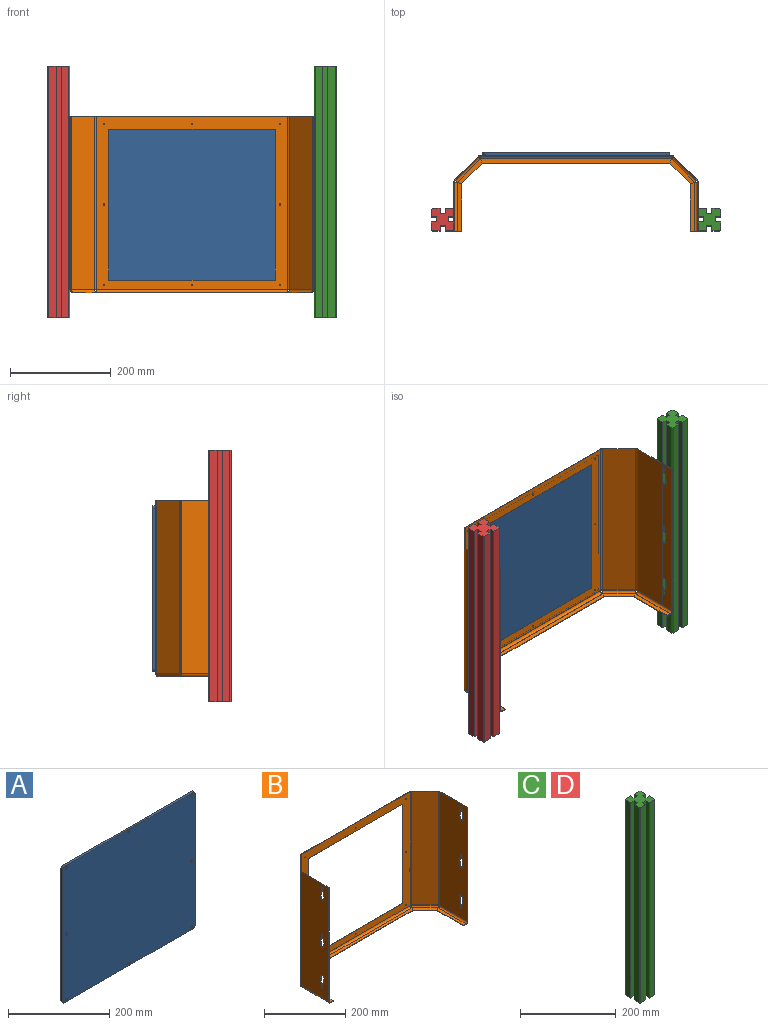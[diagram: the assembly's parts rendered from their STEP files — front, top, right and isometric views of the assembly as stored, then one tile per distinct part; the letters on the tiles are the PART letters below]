
ASSEMBLY  parts=4 mates=3
PART A: 26 faces, bbox 370x5x330 mm
  f0: plane 360x5mm, normal (0,0,-1), area 1800mm2, adj f4,f5,f22,f25
  f1: plane 320x5mm, normal (1,0,0), area 1600mm2, adj f4,f5,f22,f23
  f2: plane 360x5mm, normal (0,0,1), area 1800mm2, adj f4,f5,f23,f24
  f3: plane 320x5mm, normal (-1,0,0), area 1600mm2, adj f4,f5,f24,f25
  f4: plane 370x330mm, normal (0,-1,0), area 121794.8mm2, adj f0,f1,f2,f3,f7,f9,f11,f13
  f5: plane 370x330mm, normal (0,1,0), area 122005.9mm2, adj f0,f1,f2,f3,f6,f8,f10,f12
  f6: cylinder r=1.7mm len=3.4mm, axis (0,-1,0), area 35.7mm2, adj f5,f7
  f7: cone r=1.7mm half-angle=45deg, axis (0,-1,0), area 37.3mm2, adj f4,f6
  f8: cylinder r=1.7mm len=3.4mm, axis (0,-1,0), area 35.7mm2, adj f5,f9
  f9: cone r=1.7mm half-angle=45deg, axis (0,-1,0), area 37.3mm2, adj f4,f8
  f10: cylinder r=1.7mm len=3.4mm, axis (0,-1,0), area 35.7mm2, adj f5,f11
  f11: cone r=1.7mm half-angle=45deg, axis (0,-1,0), area 37.3mm2, adj f4,f10
  f12: cylinder r=1.7mm len=3.4mm, axis (0,-1,0), area 35.7mm2, adj f5,f13
  f13: cone r=1.7mm half-angle=45deg, axis (0,-1,0), area 37.3mm2, adj f4,f12
  f14: cylinder r=1.7mm len=3.4mm, axis (0,-1,0), area 35.7mm2, adj f5,f15
  f15: cone r=1.7mm half-angle=45deg, axis (0,-1,0), area 37.3mm2, adj f4,f14
  f16: cylinder r=1.7mm len=3.4mm, axis (0,-1,0), area 35.7mm2, adj f5,f17
  f17: cone r=1.7mm half-angle=45deg, axis (0,-1,0), area 37.3mm2, adj f4,f16
  f18: cylinder r=1.7mm len=3.4mm, axis (0,-1,0), area 35.7mm2, adj f5,f19
  f19: cone r=1.7mm half-angle=45deg, axis (0,-1,0), area 37.3mm2, adj f4,f18
  f20: cylinder r=1.7mm len=3.4mm, axis (0,-1,0), area 35.7mm2, adj f5,f21
  f21: cone r=1.7mm half-angle=45deg, axis (0,-1,0), area 37.3mm2, adj f4,f20
  f22: cylinder r=5mm len=5mm, axis (0,-1,0), area 39.3mm2, adj f0,f1,f4,f5
  f23: cylinder r=5mm len=5mm, axis (0,1,0), area 39.3mm2, adj f1,f2,f4,f5
  f24: cylinder r=5mm len=5mm, axis (0,-1,0), area 39.3mm2, adj f2,f3,f4,f5
  f25: cylinder r=5mm len=5mm, axis (0,1,0), area 39.3mm2, adj f0,f3,f4,f5
PART B: 146 faces, bbox 485x150x350 mm
  f0: plane 1.2x0.01mm, normal (0,0,-1), area 0mm2, adj f27,f28,f121,f142
  f1: plane 97.43x1.2mm, normal (0,0,1), area 116.9mm2, adj f26,f27,f28,f120
  f2: cylinder r=5mm len=4.68mm, axis (1,0,0), area 7.3mm2, adj f3,f25,f27,f28
  f3: plane 18x1.2mm, normal (0,-1,0), area 21.6mm2, adj f2,f4,f27,f28
  f4: cylinder r=5mm len=10mm, axis (1,0,0), area 18.8mm2, adj f3,f5,f27,f28
  f5: plane 18x1.2mm, normal (0,1,0), area 21.6mm2, adj f4,f6,f27,f28
  f6: cylinder r=5mm len=4.68mm, axis (1,0,0), area 7.3mm2, adj f5,f7,f27,f28
  f7: plane 10.32x1.2mm, normal (0,1,0), area 12.4mm2, adj f6,f8,f27,f28
  f8: cylinder r=1.75mm len=3.5mm, axis (1,0,0), area 6.6mm2, adj f7,f25,f27,f28
  f9: cylinder r=5mm len=4.68mm, axis (1,0,0), area 7.3mm2, adj f10,f24,f27,f28
  f10: plane 18x1.2mm, normal (0,1,0), area 21.6mm2, adj f9,f11,f27,f28
  f11: cylinder r=5mm len=10mm, axis (1,0,0), area 18.8mm2, adj f10,f12,f27,f28
  f12: plane 18x1.2mm, normal (0,-1,0), area 21.6mm2, adj f11,f13,f27,f28
  f13: cylinder r=5mm len=4.68mm, axis (1,0,0), area 7.3mm2, adj f12,f14,f27,f28
  f14: plane 10.32x1.2mm, normal (0,-1,0), area 12.4mm2, adj f13,f15,f27,f28
  f15: cylinder r=1.75mm len=3.5mm, axis (1,0,0), area 6.6mm2, adj f14,f24,f27,f28
  f16: cylinder r=5mm len=4.68mm, axis (1,0,0), area 7.3mm2, adj f17,f23,f27,f28
  f17: plane 18x1.2mm, normal (0,-1,0), area 21.6mm2, adj f16,f18,f27,f28
  f18: cylinder r=5mm len=10mm, axis (1,0,0), area 18.8mm2, adj f17,f19,f27,f28
  f19: plane 18x1.2mm, normal (0,1,0), area 21.6mm2, adj f18,f20,f27,f28
  f20: cylinder r=5mm len=4.68mm, axis (1,0,0), area 7.3mm2, adj f19,f21,f27,f28
  f21: plane 10.32x1.2mm, normal (0,1,0), area 12.4mm2, adj f20,f22,f27,f28
  f22: cylinder r=1.75mm len=3.5mm, axis (1,0,0), area 6.6mm2, adj f21,f23,f27,f28
  f23: plane 10.32x1.2mm, normal (0,-1,0), area 12.4mm2, adj f16,f22,f27,f28
  f24: plane 10.32x1.2mm, normal (0,1,0), area 12.4mm2, adj f9,f15,f27,f28
  f25: plane 10.32x1.2mm, normal (0,-1,0), area 12.4mm2, adj f2,f8,f27,f28
  f26: plane 343.8x1.2mm, normal (0,-1,0), area 412.6mm2, adj f1,f27,f28,f143
  f27: plane 343.8x97.43mm, normal (1,0,0), area 32600.9mm2, adj f0,f1,f2,f3,f4,f5,f6,f7
  f28: plane 343.8x97.43mm, normal (-1,0,0), area 32600.9mm2, adj f0,f1,f2,f3,f4,f5,f6,f7
  f29: plane 1.2x0.01mm, normal (0,0,-1), area 0mm2, adj f44,f45,f94,f133
  f30: plane 300x1.2mm, normal (1,0,0), area 360mm2, adj f31,f43,f44,f45
  f31: plane 330x1.2mm, normal (0,0,-1), area 396mm2, adj f30,f32,f44,f45
  f32: plane 300x1.2mm, normal (-1,0,0), area 360mm2, adj f31,f43,f44,f45
  f33: plane 1.2x0.01mm, normal (0,0,-1), area 0mm2, adj f44,f45,f125,f134
  f34: plane 379.86x1.2mm, normal (0,0,1), area 455.8mm2, adj f44,f45,f93,f124
  f35: cylinder r=1.25mm len=2.5mm, axis (0,-1,0), area 9.4mm2, adj f44,f45
  f36: cylinder r=1.25mm len=2.5mm, axis (0,-1,0), area 9.4mm2, adj f44,f45
  f37: cylinder r=1.25mm len=2.5mm, axis (0,-1,0), area 9.4mm2, adj f44,f45
  f38: cylinder r=1.25mm len=2.5mm, axis (0,-1,0), area 9.4mm2, adj f44,f45
  f39: cylinder r=1.25mm len=2.5mm, axis (0,-1,0), area 9.4mm2, adj f44,f45
  f40: cylinder r=1.25mm len=2.5mm, axis (0,-1,0), area 9.4mm2, adj f44,f45
  f41: cylinder r=1.25mm len=2.5mm, axis (0,-1,0), area 9.4mm2, adj f44,f45
  f42: cylinder r=1.25mm len=2.5mm, axis (0,-1,0), area 9.4mm2, adj f44,f45
  f43: plane 330x1.2mm, normal (0,0,1), area 396mm2, adj f30,f32,f44,f45
  f44: plane 379.86x343.8mm, normal (0,-1,0), area 31557.9mm2, adj f29,f30,f31,f32,f33,f34,f35,f36
  f45: plane 379.86x343.8mm, normal (0,1,0), area 31557.9mm2, adj f29,f30,f31,f32,f33,f34,f35,f36
  f46: plane 1.2x0.01mm, normal (0,0,-1), area 0mm2, adj f73,f74,f90,f103
  f47: plane 343.8x1.2mm, normal (0,-1,0), area 412.6mm2, adj f48,f73,f74,f102
  f48: plane 97.43x1.2mm, normal (0,0,1), area 116.9mm2, adj f47,f73,f74,f89
  f49: cylinder r=1.75mm len=3.5mm, axis (-1,0,0), area 6.6mm2, adj f50,f72,f73,f74
  f50: plane 10.32x1.2mm, normal (0,1,0), area 12.4mm2, adj f49,f51,f73,f74
  f51: cylinder r=5mm len=4.68mm, axis (-1,0,0), area 7.3mm2, adj f50,f52,f73,f74
  f52: plane 18x1.2mm, normal (0,1,0), area 21.6mm2, adj f51,f53,f73,f74
  f53: cylinder r=5mm len=10mm, axis (-1,0,0), area 18.8mm2, adj f52,f54,f73,f74
  f54: plane 18x1.2mm, normal (0,-1,0), area 21.6mm2, adj f53,f55,f73,f74
  f55: cylinder r=5mm len=4.68mm, axis (-1,0,0), area 7.3mm2, adj f54,f72,f73,f74
  f56: cylinder r=1.75mm len=3.5mm, axis (-1,0,0), area 6.6mm2, adj f57,f71,f73,f74
  f57: plane 10.32x1.2mm, normal (0,-1,0), area 12.4mm2, adj f56,f58,f73,f74
  f58: cylinder r=5mm len=4.68mm, axis (-1,0,0), area 7.3mm2, adj f57,f59,f73,f74
  f59: plane 18x1.2mm, normal (0,-1,0), area 21.6mm2, adj f58,f60,f73,f74
  f60: cylinder r=5mm len=10mm, axis (-1,0,0), area 18.8mm2, adj f59,f61,f73,f74
  f61: plane 18x1.2mm, normal (0,1,0), area 21.6mm2, adj f60,f62,f73,f74
  f62: cylinder r=5mm len=4.68mm, axis (-1,0,0), area 7.3mm2, adj f61,f71,f73,f74
  f63: cylinder r=1.75mm len=3.5mm, axis (-1,0,0), area 6.6mm2, adj f64,f70,f73,f74
  f64: plane 10.32x1.2mm, normal (0,1,0), area 12.4mm2, adj f63,f65,f73,f74
  f65: cylinder r=5mm len=4.68mm, axis (-1,0,0), area 7.3mm2, adj f64,f66,f73,f74
  f66: plane 18x1.2mm, normal (0,1,0), area 21.6mm2, adj f65,f67,f73,f74
  f67: cylinder r=5mm len=10mm, axis (-1,0,0), area 18.8mm2, adj f66,f68,f73,f74
  f68: plane 18x1.2mm, normal (0,-1,0), area 21.6mm2, adj f67,f69,f73,f74
  f69: cylinder r=5mm len=4.68mm, axis (-1,0,0), area 7.3mm2, adj f68,f70,f73,f74
  f70: plane 10.32x1.2mm, normal (0,-1,0), area 12.4mm2, adj f63,f69,f73,f74
  f71: plane 10.32x1.2mm, normal (0,1,0), area 12.4mm2, adj f56,f62,f73,f74
  f72: plane 10.32x1.2mm, normal (0,-1,0), area 12.4mm2, adj f49,f55,f73,f74
  f73: plane 343.8x97.43mm, normal (-1,0,0), area 32600.9mm2, adj f46,f47,f48,f49,f50,f51,f52,f53
  f74: plane 343.8x97.43mm, normal (1,0,0), area 32600.9mm2, adj f46,f47,f48,f49,f50,f51,f52,f53
  f75: plane 0.86x0.86mm, normal (0,0,-1), area 0mm2, adj f78,f79,f86,f90
  f76: plane 0.86x0.86mm, normal (0,0,-1), area 0mm2, adj f78,f79,f85,f94
  f77: plane 47.22x47.22mm, normal (0,0,1), area 78.7mm2, adj f78,f79,f89,f93
  f78: plane 343.8x46.37mm, normal (-0.71,-0.71,0), area 22544.5mm2, adj f75,f76,f77,f88,f92,f96
  f79: plane 343.8x46.37mm, normal (0.71,0.71,0), area 22544.5mm2, adj f75,f76,f77,f87,f91,f95
  f80: plane 41.2x41.2mm, normal (-0.71,-0.71,0), area 69.9mm2, adj f81,f82,f83,f84
  f81: plane 8.8x3.65mm, normal (0.38,-0.92,0), area 11.4mm2, adj f80,f83,f84,f86
  f82: plane 8.8x3.65mm, normal (-0.92,0.38,0), area 11.4mm2, adj f80,f83,f84,f85
  f83: plane 50x50mm, normal (0,0,1), area 544.8mm2, adj f80,f81,f82,f88
  f84: plane 50x50mm, normal (0,0,-1), area 544.8mm2, adj f80,f81,f82,f87
  f85: plane 6.2x4.38mm, normal (-0.71,0.71,0), area 10.6mm2, adj f76,f82,f87,f88
  f86: plane 6.2x4.38mm, normal (0.71,-0.71,0), area 10.6mm2, adj f75,f81,f87,f88
  f87: cylinder r=6.2mm len=50.74mm, axis (-0.71,0.71,0), area 638.4mm2, adj f79,f84,f85,f86
  f88: cylinder r=5mm len=49.89mm, axis (-0.71,0.71,0), area 514.9mm2, adj f78,f83,f85,f86
  f89: plane 4.38x2.66mm, normal (0,0,1), area 5.3mm2, adj f48,f77,f91,f92
  f90: plane 4.38x2.66mm, normal (0,0,-1), area 5.3mm2, adj f46,f75,f91,f92
  f91: cylinder r=6.2mm len=343.8mm, axis (0,0,1), area 1674.1mm2, adj f74,f79,f89,f90
  f92: cylinder r=5mm len=343.8mm, axis (0,0,1), area 1350.1mm2, adj f73,f78,f89,f90
  f93: plane 4.38x2.66mm, normal (0,0,1), area 5.3mm2, adj f34,f77,f95,f96
  f94: plane 4.38x2.66mm, normal (0,0,-1), area 5.3mm2, adj f29,f76,f95,f96
  f95: cylinder r=6.2mm len=343.8mm, axis (0,0,1), area 1674.1mm2, adj f45,f79,f93,f94
  f96: cylinder r=5mm len=343.8mm, axis (0,0,1), area 1350.1mm2, adj f44,f78,f93,f94
  f97: plane 93.78x1.2mm, normal (-1,0,0), area 112.5mm2, adj f98,f99,f100,f101
  f98: plane 8.8x1.2mm, normal (0,-1,0), area 10.6mm2, adj f97,f100,f101,f102
  f99: plane 8.8x3.65mm, normal (-0.38,0.92,0), area 11.4mm2, adj f97,f100,f101,f103
  f100: plane 97.42x8.8mm, normal (0,0,1), area 841.3mm2, adj f97,f98,f99,f105
  f101: plane 97.42x8.8mm, normal (0,0,-1), area 841.3mm2, adj f97,f98,f99,f104
  f102: plane 6.2x6.2mm, normal (0,-1,0), area 10.6mm2, adj f47,f98,f104,f105
  f103: plane 6.2x6.2mm, normal (0,1,0), area 10.6mm2, adj f46,f99,f104,f105
  f104: cylinder r=6.2mm len=97.42mm, axis (0,-1,0), area 948.8mm2, adj f74,f101,f102,f103
  f105: cylinder r=5mm len=97.42mm, axis (0,-1,0), area 765.1mm2, adj f73,f100,f102,f103
  f106: plane 0.86x0.86mm, normal (0,0,-1), area 0mm2, adj f109,f110,f116,f125
  f107: plane 0.86x0.86mm, normal (0,0,-1), area 0mm2, adj f109,f110,f117,f121
  f108: plane 47.22x47.22mm, normal (0,0,1), area 78.7mm2, adj f109,f110,f120,f124
  f109: plane 343.8x46.37mm, normal (0.71,-0.71,0), area 22544.5mm2, adj f106,f107,f108,f119,f123,f127
  f110: plane 343.8x46.37mm, normal (-0.71,0.71,0), area 22544.5mm2, adj f106,f107,f108,f118,f122,f126
  f111: plane 41.2x41.2mm, normal (0.71,-0.71,0), area 69.9mm2, adj f112,f113,f114,f115
  f112: plane 8.8x3.65mm, normal (0.92,0.38,0), area 11.4mm2, adj f111,f114,f115,f116
  f113: plane 8.8x3.65mm, normal (-0.38,-0.92,0), area 11.4mm2, adj f111,f114,f115,f117
  f114: plane 50x50mm, normal (0,0,1), area 544.8mm2, adj f111,f112,f113,f119
  f115: plane 50x50mm, normal (0,0,-1), area 544.8mm2, adj f111,f112,f113,f118
  f116: plane 6.2x4.38mm, normal (0.71,0.71,0), area 10.6mm2, adj f106,f112,f118,f119
  f117: plane 6.2x4.38mm, normal (-0.71,-0.71,0), area 10.6mm2, adj f107,f113,f118,f119
  f118: cylinder r=6.2mm len=50.74mm, axis (0.71,0.71,0), area 638.4mm2, adj f110,f115,f116,f117
  f119: cylinder r=5mm len=49.89mm, axis (0.71,0.71,0), area 514.9mm2, adj f109,f114,f116,f117
  f120: plane 4.38x2.66mm, normal (0,0,1), area 5.3mm2, adj f1,f108,f122,f123
  f121: plane 4.38x2.66mm, normal (0,0,-1), area 5.3mm2, adj f0,f107,f122,f123
  f122: cylinder r=6.2mm len=343.8mm, axis (0,0,1), area 1674.1mm2, adj f28,f110,f120,f121
  f123: cylinder r=5mm len=343.8mm, axis (0,0,1), area 1350.1mm2, adj f27,f109,f120,f121
  f124: plane 4.38x2.66mm, normal (0,0,1), area 5.3mm2, adj f34,f108,f126,f127
  f125: plane 4.38x2.66mm, normal (0,0,-1), area 5.3mm2, adj f33,f106,f126,f127
  f126: cylinder r=6.2mm len=343.8mm, axis (0,0,1), area 1674.1mm2, adj f45,f110,f124,f125
  f127: cylinder r=5mm len=343.8mm, axis (0,0,1), area 1350.1mm2, adj f44,f109,f124,f125
  f128: plane 372.55x1.2mm, normal (0,-1,0), area 447.1mm2, adj f129,f130,f131,f132
  f129: plane 8.8x3.65mm, normal (0.92,-0.38,0), area 11.4mm2, adj f128,f131,f132,f133
  f130: plane 8.8x3.65mm, normal (-0.92,-0.38,0), area 11.4mm2, adj f128,f131,f132,f134
  f131: plane 379.84x8.8mm, normal (0,0,1), area 3310.5mm2, adj f128,f129,f130,f136
  f132: plane 379.84x8.8mm, normal (0,0,-1), area 3310.5mm2, adj f128,f129,f130,f135
  f133: plane 6.2x6.2mm, normal (1,0,0), area 10.6mm2, adj f29,f129,f135,f136
  f134: plane 6.2x6.2mm, normal (-1,0,0), area 10.6mm2, adj f33,f130,f135,f136
  f135: cylinder r=6.2mm len=379.84mm, axis (1,0,0), area 3699.3mm2, adj f45,f132,f133,f134
  f136: cylinder r=5mm len=379.84mm, axis (1,0,0), area 2983.3mm2, adj f44,f131,f133,f134
  f137: plane 93.78x1.2mm, normal (1,0,0), area 112.5mm2, adj f138,f139,f140,f141
  f138: plane 8.8x3.65mm, normal (0.38,0.92,0), area 11.4mm2, adj f137,f140,f141,f142
  f139: plane 8.8x1.2mm, normal (0,-1,0), area 10.6mm2, adj f137,f140,f141,f143
  f140: plane 97.42x8.8mm, normal (0,0,1), area 841.3mm2, adj f137,f138,f139,f145
  f141: plane 97.42x8.8mm, normal (0,0,-1), area 841.3mm2, adj f137,f138,f139,f144
  f142: plane 6.2x6.2mm, normal (0,1,0), area 10.6mm2, adj f0,f138,f144,f145
  f143: plane 6.2x6.2mm, normal (0,-1,0), area 10.6mm2, adj f26,f139,f144,f145
  f144: cylinder r=6.2mm len=97.42mm, axis (0,1,0), area 948.8mm2, adj f28,f141,f142,f143
  f145: cylinder r=5mm len=97.42mm, axis (0,1,0), area 765.1mm2, adj f27,f140,f142,f143
PART C: 26 faces, bbox 45x45x500 mm
  f0: plane 500x15.5mm, normal (0,-1,0), area 7750mm2, adj f19,f20,f21,f22
  f1: plane 500x15.5mm, normal (1,0,0), area 7750mm2, adj f2,f20,f21,f22
  f2: plane 500x10mm, normal (0,1,0), area 5000mm2, adj f1,f3,f20,f21
  f3: plane 500x10mm, normal (1,0,0), area 5000mm2, adj f2,f4,f20,f21
  f4: plane 500x10mm, normal (0,-1,0), area 5000mm2, adj f3,f5,f20,f21
  f5: plane 500x15.5mm, normal (1,0,0), area 7750mm2, adj f4,f20,f21,f23
  f6: plane 500x15.5mm, normal (0,1,0), area 7750mm2, adj f7,f20,f21,f23
  f7: plane 500x10mm, normal (-1,0,0), area 5000mm2, adj f6,f8,f20,f21
  f8: plane 500x10mm, normal (0,1,0), area 5000mm2, adj f7,f9,f20,f21
  f9: plane 500x10mm, normal (1,0,0), area 5000mm2, adj f8,f10,f20,f21
  f10: plane 500x15.5mm, normal (0,1,0), area 7750mm2, adj f9,f20,f21,f25
  f11: plane 500x15.5mm, normal (-1,0,0), area 7750mm2, adj f12,f20,f21,f25
  f12: plane 500x10mm, normal (0,-1,0), area 5000mm2, adj f11,f13,f20,f21
  f13: plane 500x10mm, normal (-1,0,0), area 5000mm2, adj f12,f14,f20,f21
  f14: plane 500x10mm, normal (0,1,0), area 5000mm2, adj f13,f15,f20,f21
  f15: plane 500x15.5mm, normal (-1,0,0), area 7750mm2, adj f14,f20,f21,f24
  f16: plane 500x15.5mm, normal (0,-1,0), area 7750mm2, adj f17,f20,f21,f24
  f17: plane 500x10mm, normal (1,0,0), area 5000mm2, adj f16,f18,f20,f21
  f18: plane 500x10mm, normal (0,-1,0), area 5000mm2, adj f17,f19,f20,f21
  f19: plane 500x10mm, normal (-1,0,0), area 5000mm2, adj f0,f18,f20,f21
  f20: plane 45x45mm, normal (0,0,1), area 1617mm2, adj f0,f1,f2,f3,f4,f5,f6,f7
  f21: plane 45x45mm, normal (0,0,-1), area 1617mm2, adj f0,f1,f2,f3,f4,f5,f6,f7
  f22: plane 500x2mm, normal (0.71,-0.71,0), area 1414.2mm2, adj f0,f1,f20,f21
  f23: plane 500x2mm, normal (0.71,0.71,0), area 1414.2mm2, adj f5,f6,f20,f21
  f24: plane 500x2mm, normal (-0.71,-0.71,0), area 1414.2mm2, adj f15,f16,f20,f21
  f25: plane 500x2mm, normal (-0.71,0.71,0), area 1414.2mm2, adj f10,f11,f20,f21
PART D: same geometry as C
PLACE A rot(axis=(0,0,1),180deg) t=(0.14,75.37,-4.57)mm
PLACE B t=(0.14,75.37,-4.57)mm
PLACE C t=(265.14,-52.13,-229.57)mm
PLACE D t=(-264.86,-52.13,-229.57)mm
MATE fastened A.f16 <-> B.f38  axis (0,-1,0) through (175.14,75.37,155.43)mm
MATE fastened D.f1 <-> B.f28  axis (1,0,0) through (-242.36,-72.63,270.43)mm
MATE fastened C.f15 <-> B.f74  axis (-1,0,0) through (242.64,-72.63,270.43)mm
